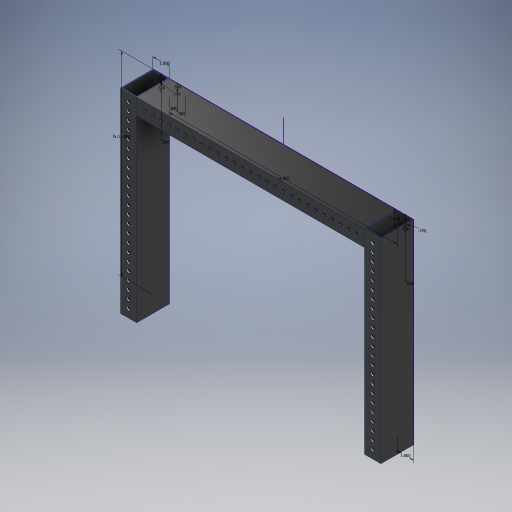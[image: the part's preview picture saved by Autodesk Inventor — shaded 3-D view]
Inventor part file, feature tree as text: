
AUTODESK INVENTOR PART (.ipt)
format: ipt  version: 2024.2 (Build 282272000, 272)  size: 558,592 bytes
history: native  units: in
note: dims shown in document units (in); Inventor stores cm internally (conversion verified against a paired STEP export)
features: extrude x9, sketch x5, projected_geometry x4, other x3
ambient origin geometry x8: Origin, YZ Plane, XZ Plane, XY Plane, X Axis, Y Axis, Z Axis, Center Point
bodies: Body1 (feature_tree), Body2 (feature_tree), Body3 (feature_tree)
feature tree (21):
  other  "2024-220-001-Right-Stop-Support"
  sketch  "Sketch1"  dims[d0=1.0in d2=14.0in]
  extrude  "Extrusion1"  Depth=14.0in
  extrude  "Extrusion2"  Depth=1.0in
  extrude  "Extrusion3"  Depth=2.0in TaperAngle=0.0deg
  extrude  "Extrusion4"  Depth=0.0625in
  extrude  "Extrusion5"  Depth=0.0625in
  extrude  "Extrusion6"  Depth=1.0in TaperAngle=0.0deg
  extrude  "Extrusion7"  Depth=0.0625in
  extrude  "Extrusion8"  Depth=11.0in TaperAngle=0.0deg
  extrude  "Extrusion9"  Depth=0.0625in
  other  "2024-220-002-Shootaur-Rest"
  other  "2024-220-003-Left-Stop-Support"
  sketch  "Sketch2"  dims[d3=1.0in d4=1.0in]
  projected_geometry  "Projected Loop1"
  sketch  "Sketch3"  dims[d32=2.0in d33=0.0in d34=2.0in d35=0.0in]
  projected_geometry  "Projected Loop2"
  sketch  "Sketch4"  dims[d36=2.0in d37=0.0in d38=0.0625in]
  projected_geometry  "Projected Loop3"
  sketch  "Sketch5"  dims[d39=12.6875in d40=0.0in d41=0.0625in d42=12.6875in d43=0.0in d44=0.0625in d45=11.0in d46=0.0in d54=0.0625in d55=4.6875in d56=0.0in d64=0.5in d65=0.5in d66=10.6299in d68=0.5in d69=0.3937in d71=1.0in d73=12.0in d75=0.196in d76=0.5in d77=0.5in d78=9.0551in d80=0.5in d81=0.3937in d83=1.0in d85=0.196in d86=0.5in d87=0.5in d88=9.0551in d90=0.5in d91=0.3937in d93=1.0in d95=2.5in d96=0.0in d97=2.5in d98=0.0in]
  projected_geometry  "Projected Loop4"
